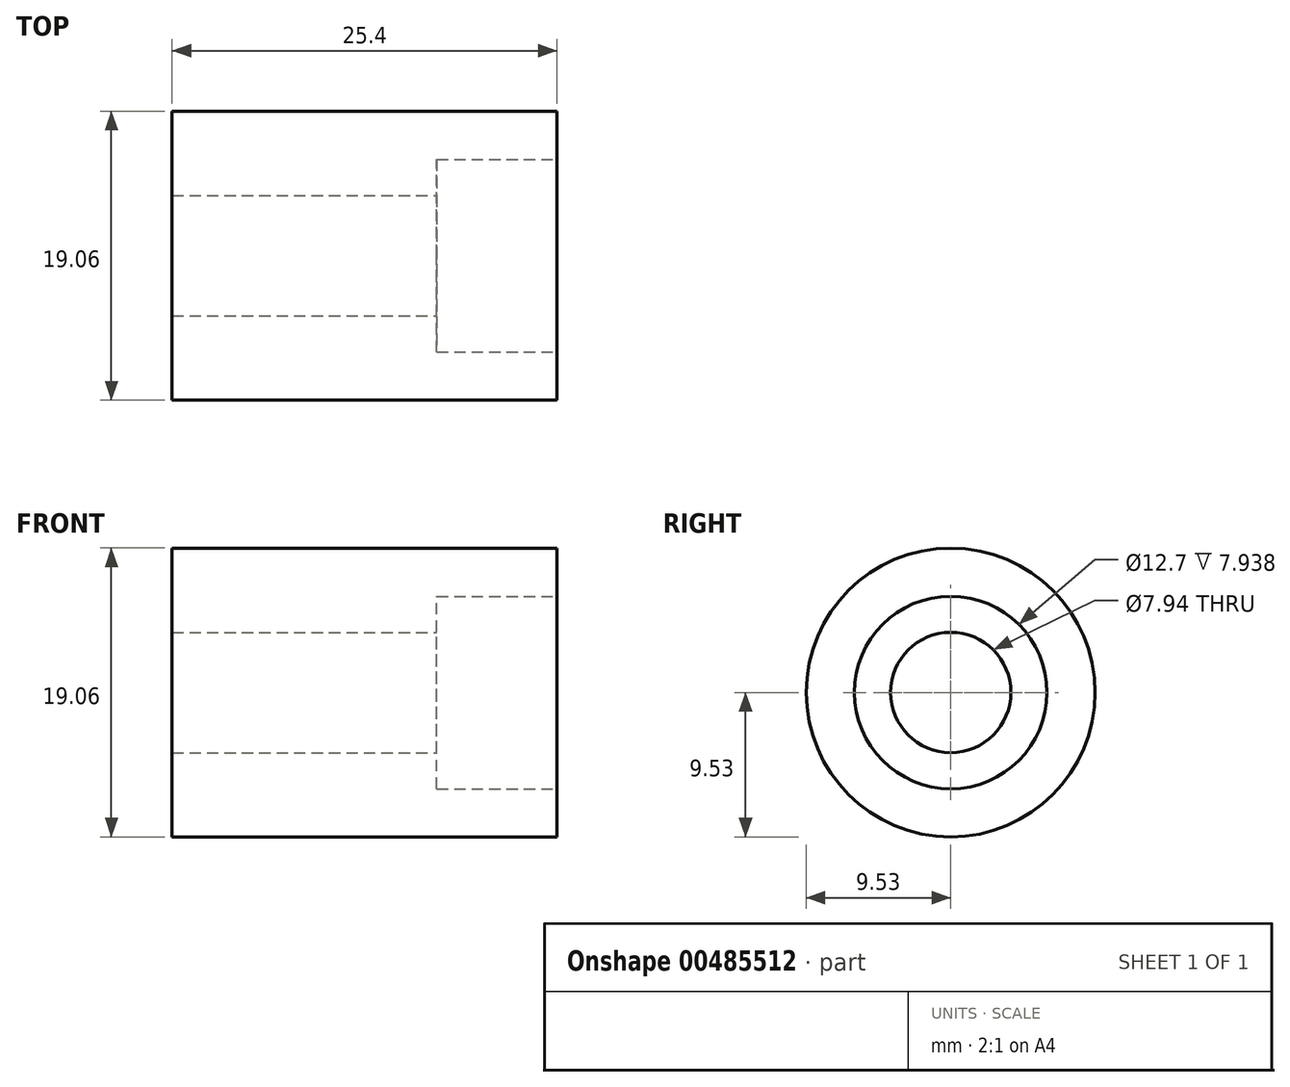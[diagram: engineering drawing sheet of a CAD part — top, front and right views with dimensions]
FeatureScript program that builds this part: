
annotation { "Feature Type Name" : "Feature", "Feature Type Description" : "" }
export const myFeature = defineFeature(function(context is Context, id is Id, definition is map)
    precondition{}
    {
        {
            var Q0;
            Q0=qCreatedBy(makeId("Right.planeOp"),FACE);
            var sketch = newSketch(context, id + "F0", { "sketchPlane" : qUnion([Q0])});
            skCircle(sketch, "E0", {"center": v(0, 0) * mm, "radius": 9.53 * mm});
            skSolve(sketch);
        }
        {
            var Q0;
            Q0 = qSketchRegion(id + "F0", true);
            extrude(context, id + "F1", {"entities" : qUnion([Q0]), "depth" : 25.4 * mm, "offsetDistance" : 25.4 * mm});
        }
        {
            var Q0;
            Q0=makeQuery(id+"F1.opExtrude","CAP_FACE",FACE,{"disambiguationData":[OSD([sQuery(id+"F0.wireOp",EDGE,"E0")])],"isStart":false});
            var sketch = newSketch(context, id + "F2", { "sketchPlane" : qUnion([Q0])});
            skCircle(sketch, "E1", {"center": v(0, 0) * mm, "radius": 6.35 * mm});
            skSolve(sketch);
        }
        {
            var Q0;
            Q0 = qSketchRegion(id + "F2", true);
            extrude(context, id + "F3", {"entities" : qUnion([Q0]), "operationType" : NewBodyOperationType.REMOVE, "oppositeDirection" : true, "depth" : 7.94 * mm, "offsetDistance" : 25.4 * mm});
        }
        {
            var Q0;
            Q0=makeQuery(id+"F3.boolean.opBoolean","COPY",FACE,{"derivedFrom":makeQuery(id+"F3.opExtrude","CAP_FACE",FACE,{"disambiguationData":[OSD([sQuery(id+"F2.wireOp",EDGE,"E1")])],"isStart":false})});
            var sketch = newSketch(context, id + "F4", { "sketchPlane" : qUnion([Q0])});
            skCircle(sketch, "E2", {"center": v(0, 0) * mm, "radius": 3.97 * mm});
            skSolve(sketch);
        }
        {
            var Q0;
            Q0 = qSketchRegion(id + "F4", true);
            extrude(context, id + "F5", {"entities" : qUnion([Q0]), "operationType" : NewBodyOperationType.REMOVE, "endBound" : BoundingType.THROUGH_ALL, "oppositeDirection" : true, "depth" : 25.4 * mm, "offsetDistance" : 25.4 * mm});
        }
    });
